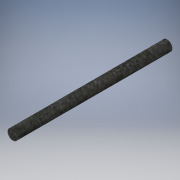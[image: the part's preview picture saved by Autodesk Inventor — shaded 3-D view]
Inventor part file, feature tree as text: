
AUTODESK INVENTOR PART (.ipt)
format: ipt  version: 2018 (Build 220112000, 112)  size: 96,768 bytes
history: native  units: mm
features: extrude x1, sketch x1
ambient origin geometry x8: Origin, YZ Plane, XZ Plane, XY Plane, X Axis, Y Axis, Z Axis, Center Point
bodies: Volumenkörper1 (feature_tree)
feature tree (2):
  extrude  "Extrusion1"  Depth=75.0mm TaperAngle=0.0deg
  sketch  "Skizze1"  dims[d0=5.0mm d1=75.0mm d2=0.0mm]
